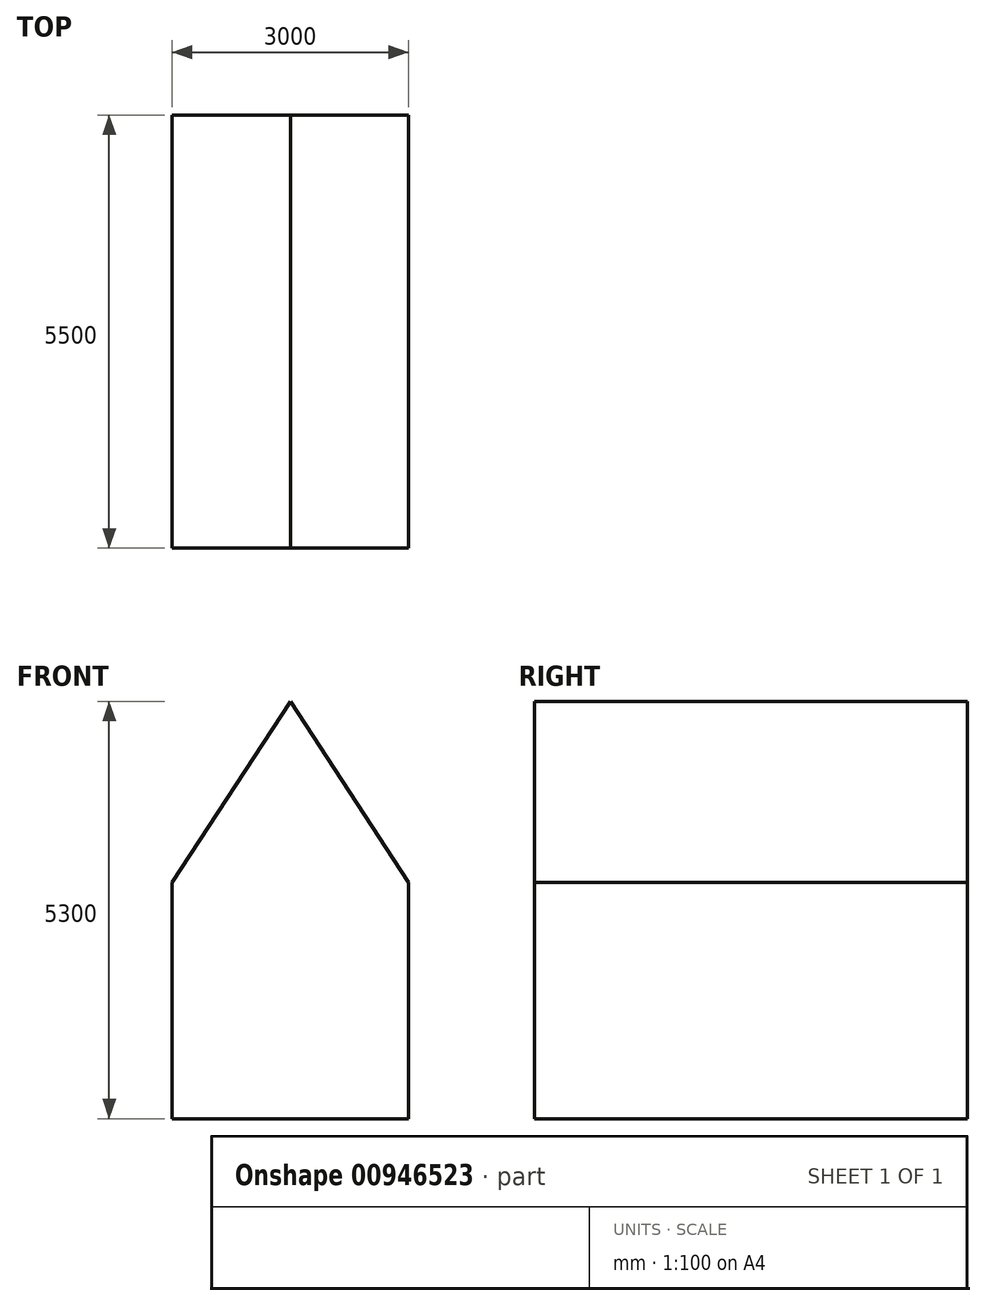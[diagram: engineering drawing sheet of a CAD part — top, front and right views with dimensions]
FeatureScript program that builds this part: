
annotation { "Feature Type Name" : "Feature", "Feature Type Description" : "" }
export const myFeature = defineFeature(function(context is Context, id is Id, definition is map)
    precondition{}
    {
        {
            var Q0;
            Q0=qCreatedBy(makeId("Front.planeOp"),FACE);
            var sketch = newSketch(context, id + "F0", { "sketchPlane" : qUnion([Q0])});
            skLineSegment(sketch, "E0.bottom", {"start": v(0, 0) * mm, "end": v(3000, 0) * mm});
            skLineSegment(sketch, "E0.left", {"start": v(0, 0) * mm, "end": v(0, 3000) * mm});
            skLineSegment(sketch, "E0.right", {"start": v(3000, 0) * mm, "end": v(3000, 3000) * mm});
            skLineSegment(sketch, "E1", {"start": v(1500, 5300) * mm, "end": v(0, 3000) * mm});
            skLineSegment(sketch, "E2", {"start": v(1500, 5300) * mm, "end": v(3000, 3000) * mm});
            skSolve(sketch);
        }
        {
            var Q0;
            Q0=makeQuery(id+"F0.imprint","IMPRINT",FACE,{"disambiguationData":[TD([[makeQuery(id+"F0.imprint","IMPRINT",EDGE,{"derivedFrom":sQuery(id+"F0.wireOp",EDGE,"E0.bottom")}),1.0]])]});
            extrude(context, id + "F1", {"entities" : qUnion([Q0]), "oppositeDirection" : true, "depth" : 5500 * mm, "offsetDistance" : 25 * mm});
        }
    });
